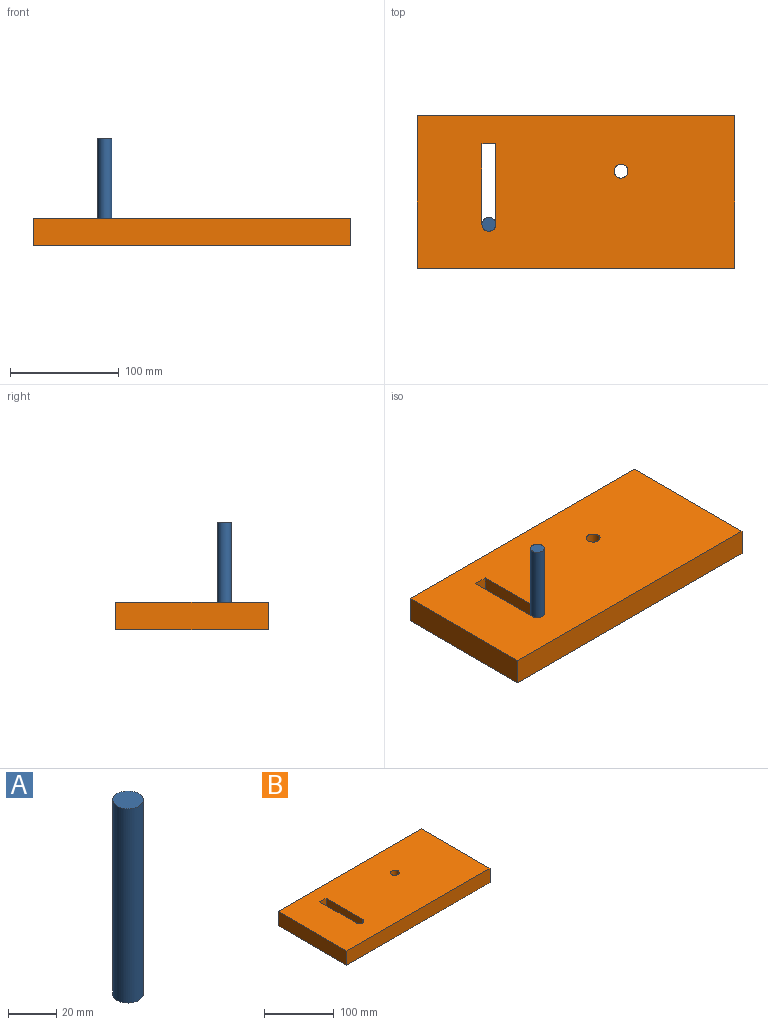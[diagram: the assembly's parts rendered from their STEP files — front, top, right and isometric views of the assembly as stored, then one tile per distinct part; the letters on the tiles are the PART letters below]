
ASSEMBLY  parts=2 mates=1
PART A: 3 faces, bbox 12.7x12.7x98.5 mm
  f0: cylinder r=6.35mm len=98.5mm, axis (0,0,-1), area 3931.8mm2, adj f1,f2
  f1: plane 12.71x12.71mm, normal (0,0,1), area 126.8mm2, adj f0
  f2: plane 12.71x12.71mm, normal (0,0,-1), area 126.8mm2, adj f0
PART B: 11 faces, bbox 291.2x139.9x25 mm
  f0: plane 291.19x25mm, normal (0,1,0), area 7279.6mm2, adj f1,f8,f9,f10
  f1: plane 139.94x25mm, normal (-1,0,0), area 3498.5mm2, adj f0,f2,f9,f10
  f2: plane 291.19x25mm, normal (0,-1,0), area 7279.6mm2, adj f1,f8,f9,f10
  f3: plane 25x12.71mm, normal (0,-1,0), area 317.6mm2, adj f4,f6,f9,f10
  f4: plane 74.07x25mm, normal (-1,0,0), area 1851.7mm2, adj f3,f5,f9,f10
  f5: cylinder r=6.35mm len=25mm, axis (0,0,-1), area 499mm2, adj f4,f6,f9,f10
  f6: plane 74.07x25mm, normal (1,0,0), area 1851.7mm2, adj f3,f5,f9,f10
  f7: cylinder r=6.35mm len=25mm, axis (0,0,-1), area 997.9mm2, adj f9,f10
  f8: plane 139.94x25mm, normal (1,0,0), area 3498.5mm2, adj f0,f2,f9,f10
  f9: plane 291.19x139.94mm, normal (0,0,1), area 39616.7mm2, adj f0,f1,f2,f3,f4,f5,f6,f7
  f10: plane 291.19x139.94mm, normal (0,0,-1), area 39616.7mm2, adj f0,f1,f2,f3,f4,f5,f6,f7
PLACE A rot(axis=(0,0,1),139.4deg) t=(-111.07,-15.22,0)mm
PLACE B at identity fixed
MATE planar B.f10 <-> A.f0  axis (0,0,-1) through (29.18,1.52,0)mm
